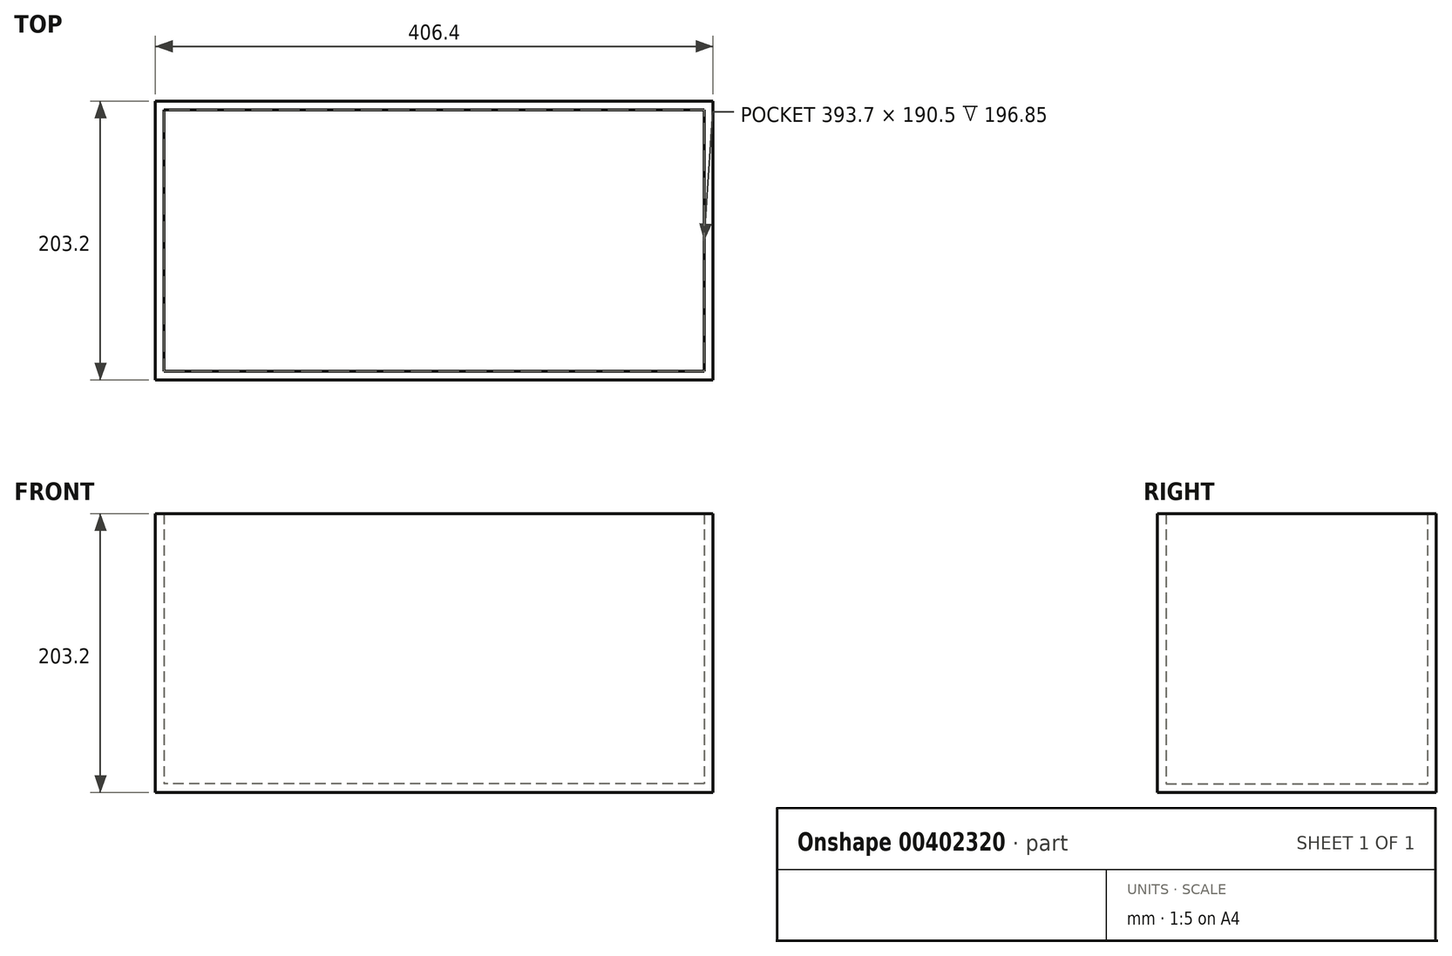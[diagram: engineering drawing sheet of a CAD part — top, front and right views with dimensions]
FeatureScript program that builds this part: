
annotation { "Feature Type Name" : "Feature", "Feature Type Description" : "" }
export const myFeature = defineFeature(function(context is Context, id is Id, definition is map)
    precondition{}
    {
        {
            var Q0;
            Q0=qCreatedBy(makeId("Front.planeOp"),FACE);
            var sketch = newSketch(context, id + "F0", { "sketchPlane" : qUnion([Q0])});
            skLineSegment(sketch, "E0.bottom", {"start": v(203.2, 101.6) * mm, "end": v(-203.2, 101.6) * mm});
            skLineSegment(sketch, "E0.top", {"start": v(203.2, -101.6) * mm, "end": v(-203.2, -101.6) * mm});
            skLineSegment(sketch, "E0.left", {"start": v(203.2, 101.6) * mm, "end": v(203.2, -101.6) * mm});
            skLineSegment(sketch, "E0.right", {"start": v(-203.2, 101.6) * mm, "end": v(-203.2, -101.6) * mm});
            skPoint(sketch, "E0.middle", {"position": v(0, 0) * mm});
            skSolve(sketch);
        }
        {
            var Q0;
            Q0 = qSketchRegion(id + "F0", true);
            extrude(context, id + "F1", {"entities" : qUnion([Q0]), "depth" : 203.2 * mm, "symmetric" : true});
        }
        {
            var Q0;
            Q0=makeQuery(id+"F1.opExtrude","SWEPT_FACE",FACE,{"disambiguationData":[OSD([sQuery(id+"F0.wireOp",EDGE,"E0.bottom")])]});
            shell(context, id + "F2", {"entities" : qUnion([Q0]), "thickness" : 6.35 * mm});
        }
    });
